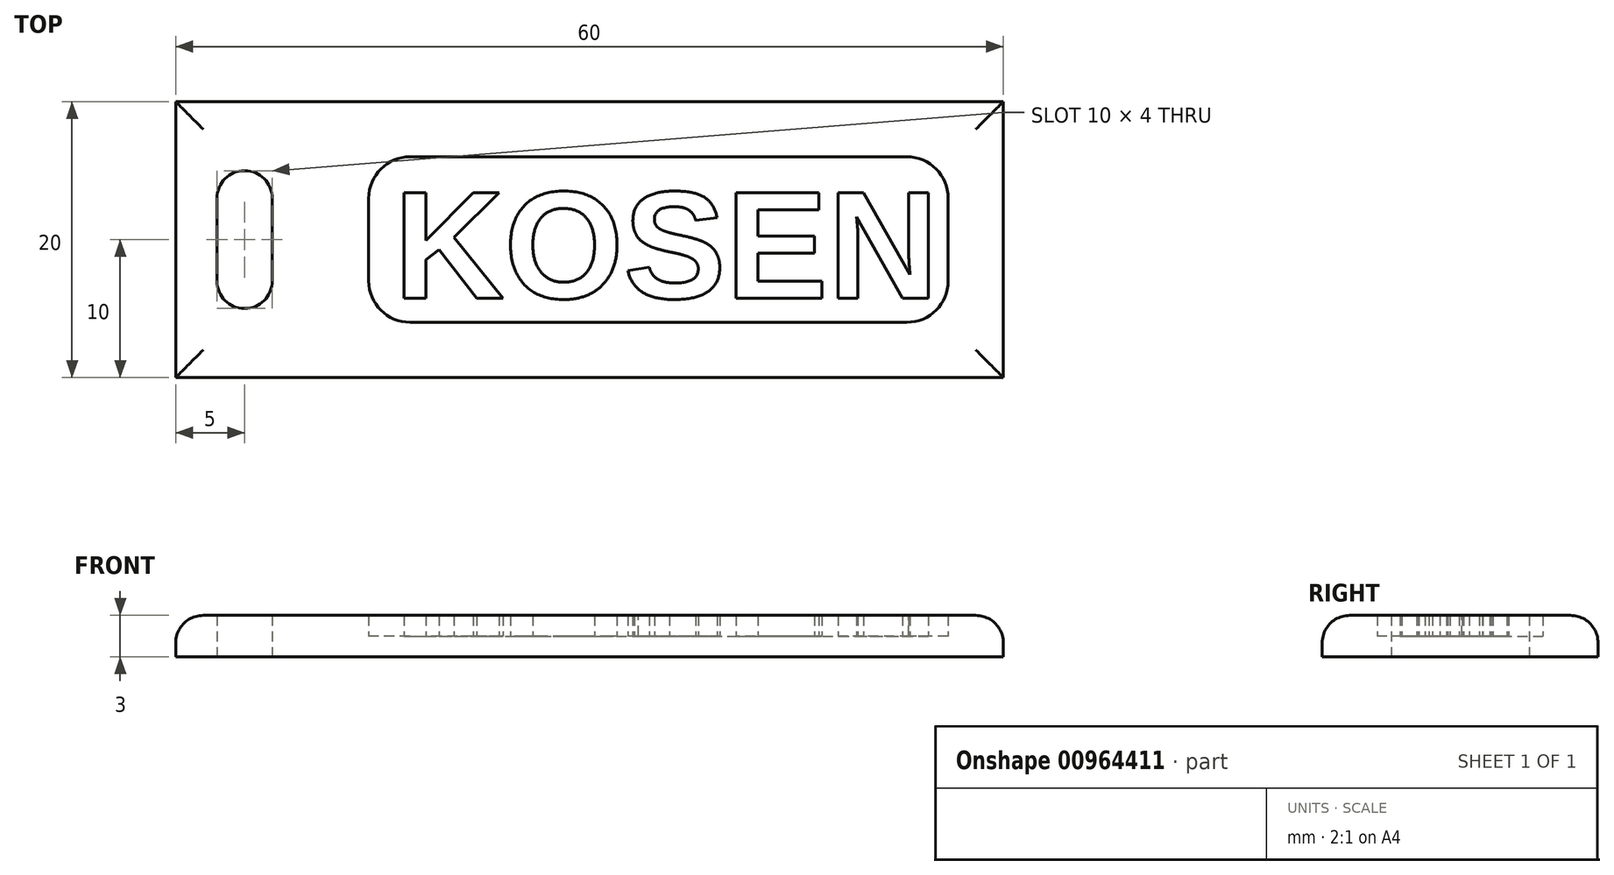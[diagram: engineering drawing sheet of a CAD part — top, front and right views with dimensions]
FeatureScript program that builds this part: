
annotation { "Feature Type Name" : "Feature", "Feature Type Description" : "" }
export const myFeature = defineFeature(function(context is Context, id is Id, definition is map)
    precondition{}
    {
        {
            var Q0;
            Q0=qCreatedBy(makeId("Top.planeOp"),FACE);
            var sketch = newSketch(context, id + "F0", { "sketchPlane" : qUnion([Q0])});
            skLineSegment(sketch, "E0.bottom", {"start": v(-25, 10) * mm, "end": v(25, 10) * mm});
            skLineSegment(sketch, "E0.top", {"start": v(-25, -10) * mm, "end": v(25, -10) * mm});
            skLineSegment(sketch, "E0.left", {"start": v(-25, 10) * mm, "end": v(-25, -10) * mm});
            skLineSegment(sketch, "E0.right", {"start": v(25, 10) * mm, "end": v(25, -10) * mm});
            skPoint(sketch, "E0.middle", {"position": v(0, 0) * mm});
            skLineSegment(sketch, "E1.bottom", {"start": v(-25, 10) * mm, "end": v(-35, 10) * mm});
            skLineSegment(sketch, "E1.top", {"start": v(-25, -10) * mm, "end": v(-35, -10) * mm});
            skLineSegment(sketch, "E1.right", {"start": v(-35, 10) * mm, "end": v(-35, -10) * mm});
            skPoint(sketch, "E1.middle", {"position": v(-30, 0) * mm});
            skPoint(sketch, "E1.middle.positionSnap0", {"position": v(-25, 0) * mm});
            skPoint(sketch, "E1.centerSnap0", {"position": v(-25, 0) * mm});
            skLineSegment(sketch, "E2.bottom", {"start": v(-30, 5) * mm, "end": v(-30, 5) * mm});
            skLineSegment(sketch, "E2.top", {"start": v(-30, -5) * mm, "end": v(-30, -5) * mm});
            skLineSegment(sketch, "E2.left", {"start": v(-32, 3) * mm, "end": v(-32, -3) * mm});
            skLineSegment(sketch, "E2.right", {"start": v(-28, 3) * mm, "end": v(-28, -3) * mm});
            skPoint(sketch, "E3.visualSharp", {"position": v(-32, 5) * mm});
            skArc(sketch, "E3.filletArc", {"start": v(-30, 5) * mm, "mid": v(-31.41, 4.41) * mm, "end": v(-32, 3) * mm});
            skPoint(sketch, "E4.visualSharp", {"position": v(-28, 5) * mm});
            skArc(sketch, "E4.filletArc", {"start": v(-28, 3) * mm, "mid": v(-28.59, 4.41) * mm, "end": v(-30, 5) * mm});
            skPoint(sketch, "E5.visualSharp", {"position": v(-28, -5) * mm});
            skArc(sketch, "E5.filletArc", {"start": v(-30, -5) * mm, "mid": v(-28.59, -4.41) * mm, "end": v(-28, -3) * mm});
            skPoint(sketch, "E6.visualSharp", {"position": v(-32, -5) * mm});
            skArc(sketch, "E6.filletArc", {"start": v(-32, -3) * mm, "mid": v(-31.41, -4.41) * mm, "end": v(-30, -5) * mm});
            skSolve(sketch);
        }
        {
            var Q0;
            Q0=qSketchRegion(id+"F0",true);
            extrude(context, id + "F1", {"entities" : qUnion([Q0]), "depth" : 3 * mm, "offsetDistance" : 25 * mm});
        }
        {
            var Q0;
            Q0=qCreatedBy(makeId("Top.planeOp"),FACE);
            var sketch = newSketch(context, id + "F2", { "sketchPlane" : qUnion([Q0])});
            skLineSegment(sketch, "E7.bottom", {"start": v(-18, 6) * mm, "end": v(18, 6) * mm});
            skLineSegment(sketch, "E7.top", {"start": v(-18, -6) * mm, "end": v(18, -6) * mm});
            skLineSegment(sketch, "E7.left", {"start": v(-21, 3) * mm, "end": v(-21, -3) * mm});
            skLineSegment(sketch, "E7.right", {"start": v(21, 3) * mm, "end": v(21, -3) * mm});
            skPoint(sketch, "E7.middle", {"position": v(0, 0) * mm});
            skPoint(sketch, "E8.visualSharp", {"position": v(-21, 6) * mm});
            skArc(sketch, "E8.filletArc", {"start": v(-18, 6) * mm, "mid": v(-20.12, 5.12) * mm, "end": v(-21, 3) * mm});
            skPoint(sketch, "E9.visualSharp", {"position": v(21, 6) * mm});
            skArc(sketch, "E9.filletArc", {"start": v(21, 3) * mm, "mid": v(20.12, 5.12) * mm, "end": v(18, 6) * mm});
            skPoint(sketch, "E10.visualSharp", {"position": v(21, -6) * mm});
            skArc(sketch, "E10.filletArc", {"start": v(18, -6) * mm, "mid": v(20.12, -5.12) * mm, "end": v(21, -3) * mm});
            skPoint(sketch, "E11.visualSharp", {"position": v(-21, -6) * mm});
            skArc(sketch, "E11.filletArc", {"start": v(-21, -3) * mm, "mid": v(-20.12, -5.12) * mm, "end": v(-18, -6) * mm});
            skSolve(sketch);
        }
        {
            var Q0;
            Q0=qSketchRegion(id+"F2",true);
            extrude(context, id + "F3", {"entities" : qUnion([Q0]), "depth" : 3 * mm, "offsetDistance" : 25 * mm});
        }
        {
            var Q0;
            Q0=makeQuery(id+"F3.opExtrude","SWEPT_BODY",BODY,{"disambiguationData":[OSD([sQuery(id+"F2.wireOp",EDGE,"E7.bottom"),sQuery(id+"F2.wireOp",EDGE,"E7.top"),sQuery(id+"F2.wireOp",EDGE,"E7.left"),sQuery(id+"F2.wireOp",EDGE,"E7.right"),sQuery(id+"F2.wireOp",EDGE,"E8.filletArc"),sQuery(id+"F2.wireOp",EDGE,"E9.filletArc"),sQuery(id+"F2.wireOp",EDGE,"E10.filletArc"),sQuery(id+"F2.wireOp",EDGE,"E11.filletArc")])]});
            transform(context, id + "F4", {"entities" : qUnion([Q0]), "transformType" : TransformType.TRANSLATION_3D, "dx" : 0 * mm, "dy" : 0 * mm, "dz" : 1.5 * mm, "makeCopy" : false});
        }
        {
            var Q0;
            Q0=makeQuery(id+"F3.opExtrude","SWEPT_BODY",BODY,{"disambiguationData":[OSD([sQuery(id+"F2.wireOp",EDGE,"E7.bottom"),sQuery(id+"F2.wireOp",EDGE,"E7.top"),sQuery(id+"F2.wireOp",EDGE,"E7.left"),sQuery(id+"F2.wireOp",EDGE,"E7.right"),sQuery(id+"F2.wireOp",EDGE,"E8.filletArc"),sQuery(id+"F2.wireOp",EDGE,"E9.filletArc"),sQuery(id+"F2.wireOp",EDGE,"E10.filletArc"),sQuery(id+"F2.wireOp",EDGE,"E11.filletArc")])]});
            var Q1;
            Q1=makeQuery(id+"F1.opExtrude","SWEPT_BODY",BODY,{"disambiguationData":[OSD([sQuery(id+"F0.wireOp",EDGE,"E0.bottom"),sQuery(id+"F0.wireOp",EDGE,"E0.top"),sQuery(id+"F0.wireOp",EDGE,"E0.right"),sQuery(id+"F0.wireOp",EDGE,"E1.bottom"),sQuery(id+"F0.wireOp",EDGE,"E1.top"),sQuery(id+"F0.wireOp",EDGE,"E1.right"),sQuery(id+"F0.wireOp",EDGE,"E2.left"),sQuery(id+"F0.wireOp",EDGE,"E2.right"),sQuery(id+"F0.wireOp",EDGE,"E3.filletArc"),sQuery(id+"F0.wireOp",EDGE,"E4.filletArc"),sQuery(id+"F0.wireOp",EDGE,"E5.filletArc"),sQuery(id+"F0.wireOp",EDGE,"E6.filletArc")])]});
            booleanBodies(context, id + "F5", {"operationType" : BooleanOperationType.SUBTRACTION, "tools" : qUnion([Q0]), "targets" : qUnion([Q1])});
        }
        {
            var Q0;
            Q0=qCreatedBy(makeId("Top.planeOp"),FACE);
            var sketch = newSketch(context, id + "F6", { "sketchPlane" : qUnion([Q0])});
            skText(sketch, "E12", { "text": "KOSEN", "fontName": "Arimo-Bold.ttf"});
            const initialGuessF6  = {"E12": [-0.0192, -0.00424, 1, 0, 0.008]};
            skSetInitialGuess(sketch, initialGuessF6);
            skSolve(sketch);
        }
        {
            var Q0;
            Q0 = qSketchRegion(id + "F6", true);
            extrude(context, id + "F7", {"entities" : qUnion([Q0]), "operationType" : NewBodyOperationType.ADD, "depth" : 3 * mm, "offsetDistance" : 25 * mm});
        }
        {
            var Q0;
            Q0=makeQuery(id+"F1.opExtrude","CAP_EDGE",EDGE,{"disambiguationData":[OSD([sQuery(id+"F0.wireOp",EDGE,"E0.bottom"),sQuery(id+"F0.wireOp",EDGE,"E1.bottom")])],"isStart":false});
            var Q1;
            Q1=makeQuery(id+"F1.opExtrude","CAP_EDGE",EDGE,{"disambiguationData":[OSD([sQuery(id+"F0.wireOp",EDGE,"E1.right")])],"isStart":false});
            var Q2;
            Q2=makeQuery(id+"F1.opExtrude","CAP_EDGE",EDGE,{"disambiguationData":[OSD([sQuery(id+"F0.wireOp",EDGE,"E0.top"),sQuery(id+"F0.wireOp",EDGE,"E1.top")])],"isStart":false});
            var Q3;
            Q3=makeQuery(id+"F1.opExtrude","CAP_EDGE",EDGE,{"disambiguationData":[OSD([sQuery(id+"F0.wireOp",EDGE,"E0.right")])],"isStart":false});
            fillet(context, id + "F8", {"entities" : qUnion([Q0, Q1, Q2, Q3]), "radius" : 2 * mm, "tangentPropagation" : true, "allowEdgeOverflow" : false});
        }
    });
